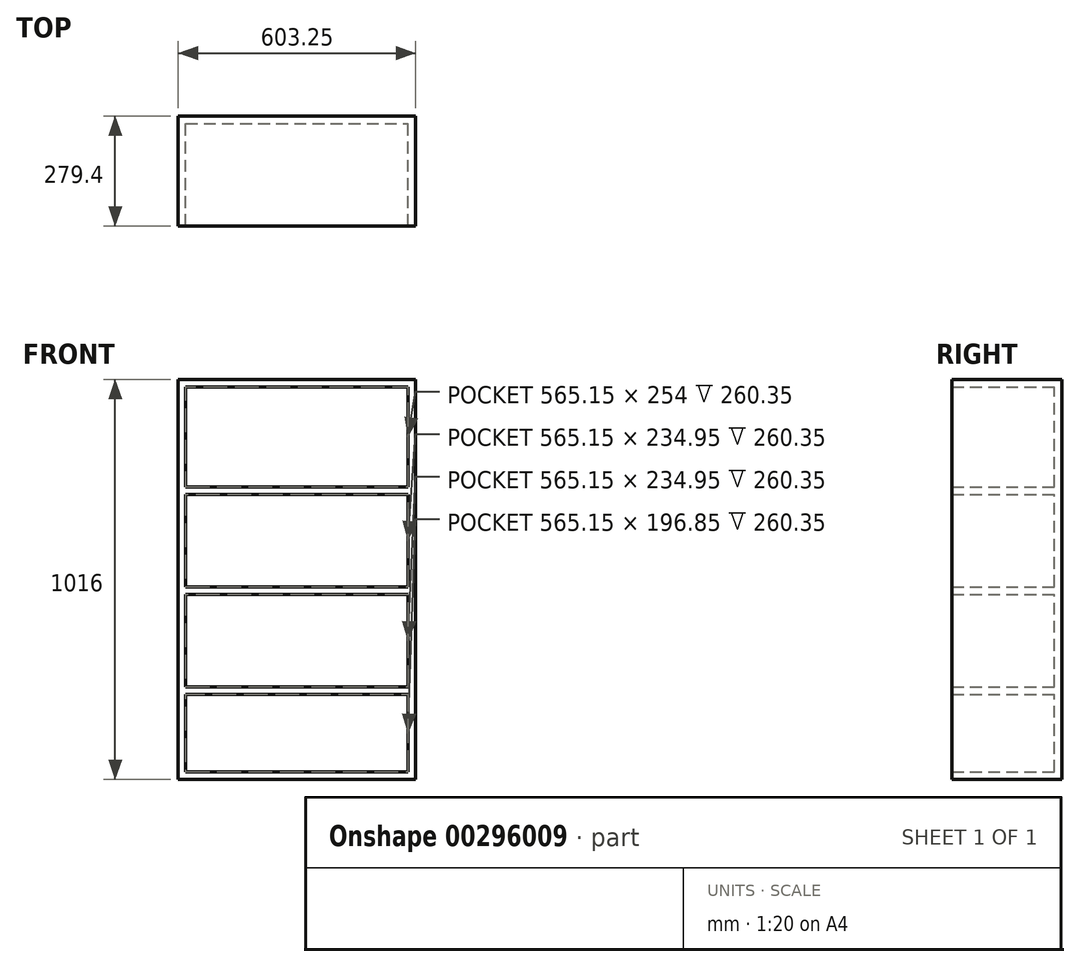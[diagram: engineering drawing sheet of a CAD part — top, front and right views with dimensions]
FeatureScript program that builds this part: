
annotation { "Feature Type Name" : "Feature", "Feature Type Description" : "" }
export const myFeature = defineFeature(function(context is Context, id is Id, definition is map)
    precondition{}
    {
        {
            var Q0;
            Q0=qCreatedBy(makeId("Front.planeOp"),FACE);
            var sketch = newSketch(context, id + "F0", { "sketchPlane" : qUnion([Q0])});
            skLineSegment(sketch, "E0.bottom", {"start": v(0, 0) * mm, "end": v(603.25, 0) * mm});
            skLineSegment(sketch, "E0.top", {"start": v(0, 1016) * mm, "end": v(603.25, 1016) * mm});
            skLineSegment(sketch, "E0.left", {"start": v(0, 0) * mm, "end": v(0, 1016) * mm});
            skLineSegment(sketch, "E0.right", {"start": v(603.25, 0) * mm, "end": v(603.25, 1016) * mm});
            skSolve(sketch);
        }
        {
            var Q0;
            Q0=qSketchRegion(id+"F0",true);
            extrude(context, id + "F1", {"entities" : qUnion([Q0]), "flatOperationType" : FlatOperationType.REMOVE, "offsetDistance" : 25.4 * mm, "depth" : 279.4 * mm, "domain" : OperationDomain.MODEL});
        }
        {
            var Q0;
            Q0=makeQuery(id+"F1.opExtrude","CAP_FACE",FACE,{"disambiguationData":[OSD([sQuery(id+"F0.wireOp",EDGE,"E0.bottom"),sQuery(id+"F0.wireOp",EDGE,"E0.top"),sQuery(id+"F0.wireOp",EDGE,"E0.left"),sQuery(id+"F0.wireOp",EDGE,"E0.right")])],"isStart":false});
            shell(context, id + "F2", {"entities" : qUnion([Q0]), "thickness" : 19.05 * mm});
        }
        {
            var Q0;
            Q0=makeQuery(id+"F2.opShell","OFFSET_FACE",FACE,{"disambiguationData":[OSD([sQuery(id+"F0.wireOp",EDGE,"E0.bottom"),sQuery(id+"F0.wireOp",EDGE,"E0.top"),sQuery(id+"F0.wireOp",EDGE,"E0.left"),sQuery(id+"F0.wireOp",EDGE,"E0.right")])]});
            var sketch = newSketch(context, id + "F3", { "sketchPlane" : qUnion([Q0])});
            skLineSegment(sketch, "E1.bottom", {"start": v(19.05, 742.95) * mm, "end": v(584.2, 742.95) * mm});
            skLineSegment(sketch, "E1.top", {"start": v(19.05, 723.9) * mm, "end": v(584.2, 723.9) * mm});
            skLineSegment(sketch, "E1.left", {"start": v(19.05, 742.95) * mm, "end": v(19.05, 723.9) * mm});
            skLineSegment(sketch, "E1.right", {"start": v(584.2, 742.95) * mm, "end": v(584.2, 723.9) * mm});
            skLineSegment(sketch, "E2.0.1.0", {"start": v(19.05, 488.95) * mm, "end": v(584.2, 488.95) * mm});
            skLineSegment(sketch, "E2.0.1.1", {"start": v(19.05, 469.9) * mm, "end": v(584.2, 469.9) * mm});
            skLineSegment(sketch, "E2.0.1.2", {"start": v(19.05, 488.95) * mm, "end": v(19.05, 469.9) * mm});
            skLineSegment(sketch, "E2.0.1.3", {"start": v(584.2, 488.95) * mm, "end": v(584.2, 469.9) * mm});
            skLineSegment(sketch, "E2.0.2.0", {"start": v(19.05, 234.95) * mm, "end": v(584.2, 234.95) * mm});
            skLineSegment(sketch, "E2.0.2.1", {"start": v(19.05, 215.9) * mm, "end": v(584.2, 215.9) * mm});
            skLineSegment(sketch, "E2.0.2.2", {"start": v(19.05, 234.95) * mm, "end": v(19.05, 215.9) * mm});
            skLineSegment(sketch, "E2.0.2.3", {"start": v(584.2, 234.95) * mm, "end": v(584.2, 215.9) * mm});
            skLineSegment(sketch, "E2.direction1", {"start": v(19.05, 723.9) * mm, "end": v(30.97, 723.9) * mm, "construction": true});
            skLineSegment(sketch, "E2.direction2", {"start": v(19.05, 723.9) * mm, "end": v(19.05, 469.9) * mm, "construction": true});
            skSolve(sketch);
        }
        {
            var Q0;
            Q0=qSketchRegion(id+"F3",true);
            extrude(context, id + "F4", {"entities" : qUnion([Q0]), "operationType" : NewBodyOperationType.ADD, "flatOperationType" : FlatOperationType.REMOVE, "offsetDistance" : 25.4 * mm, "depth" : 260.35 * mm, "domain" : OperationDomain.MODEL});
        }
    });
